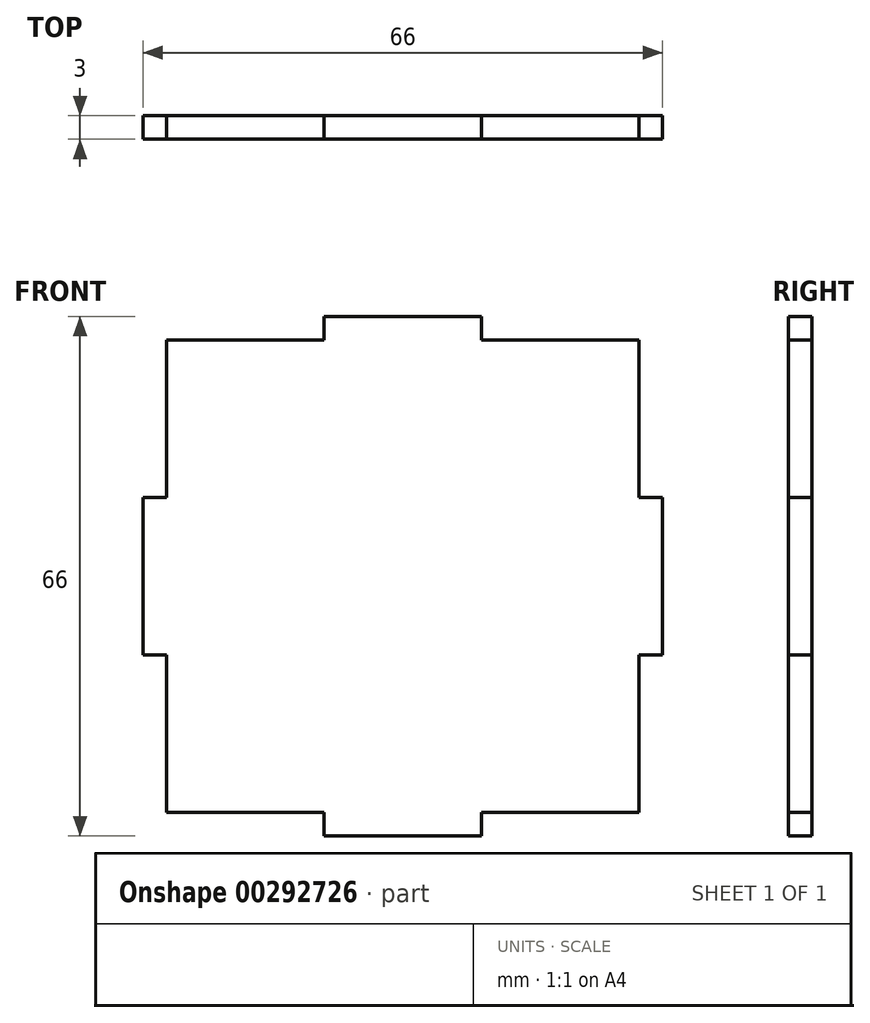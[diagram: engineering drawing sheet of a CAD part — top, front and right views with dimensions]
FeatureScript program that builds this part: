
annotation { "Feature Type Name" : "Feature", "Feature Type Description" : "" }
export const myFeature = defineFeature(function(context is Context, id is Id, definition is map)
    precondition{}
    {
        {
            var Q0;
            Q0=qCreatedBy(makeId("Front.planeOp"),FACE);
            var sketch = newSketch(context, id + "F0", { "sketchPlane" : qUnion([Q0])});
            skLineSegment(sketch, "E0", {"start": v(-33, 0) * mm, "end": v(-33, 10) * mm});
            skLineSegment(sketch, "E1", {"start": v(-33, 10) * mm, "end": v(-30, 10) * mm});
            skLineSegment(sketch, "E2", {"start": v(-30, 10) * mm, "end": v(-30, 30) * mm});
            skLineSegment(sketch, "E3", {"start": v(-30, 30) * mm, "end": v(-10, 30) * mm});
            skLineSegment(sketch, "E4", {"start": v(-10, 30) * mm, "end": v(-10, 33) * mm});
            skLineSegment(sketch, "E5", {"start": v(-10, 33) * mm, "end": v(0, 33) * mm});
            skLineSegment(sketch, "E6.MirrorCS", {"start": v(10, 30) * mm, "end": v(10, 33) * mm});
            skLineSegment(sketch, "E7.MirrorCS", {"start": v(33, 10) * mm, "end": v(30, 10) * mm});
            skLineSegment(sketch, "E8.MirrorCS", {"start": v(33, 0) * mm, "end": v(33, 10) * mm});
            skLineSegment(sketch, "E9.MirrorCS", {"start": v(10, 33) * mm, "end": v(0, 33) * mm});
            skLineSegment(sketch, "E10.MirrorCS", {"start": v(30, 30) * mm, "end": v(10, 30) * mm});
            skLineSegment(sketch, "E11.MirrorCS", {"start": v(30, 10) * mm, "end": v(30, 30) * mm});
            skLineSegment(sketch, "E12.MirrorCS", {"start": v(10, -30) * mm, "end": v(10, -33) * mm});
            skLineSegment(sketch, "E13.MirrorCS", {"start": v(-10, -30) * mm, "end": v(-10, -33) * mm});
            skLineSegment(sketch, "E14.MirrorCS", {"start": v(-33, -10) * mm, "end": v(-30, -10) * mm});
            skLineSegment(sketch, "E15.MirrorCS", {"start": v(33, -10) * mm, "end": v(30, -10) * mm});
            skLineSegment(sketch, "E16.MirrorCS", {"start": v(-10, -33) * mm, "end": v(0, -33) * mm});
            skLineSegment(sketch, "E17.MirrorCS", {"start": v(-30, -30) * mm, "end": v(-10, -30) * mm});
            skLineSegment(sketch, "E18.MirrorCS", {"start": v(-30, -10) * mm, "end": v(-30, -30) * mm});
            skLineSegment(sketch, "E19.MirrorCS", {"start": v(-33, 0) * mm, "end": v(-33, -10) * mm});
            skLineSegment(sketch, "E20.MirrorCS", {"start": v(30, -30) * mm, "end": v(10, -30) * mm});
            skLineSegment(sketch, "E21.MirrorCS", {"start": v(30, -10) * mm, "end": v(30, -30) * mm});
            skLineSegment(sketch, "E22.MirrorCS", {"start": v(10, -33) * mm, "end": v(0, -33) * mm});
            skLineSegment(sketch, "E23.MirrorCS", {"start": v(33, 0) * mm, "end": v(33, -10) * mm});
            skSolve(sketch);
        }
        {
            var Q0;
            Q0 = qSketchRegion(id + "F0", true);
            extrude(context, id + "F1", {"entities" : qUnion([Q0]), "depth" : 3 * mm});
        }
    });
